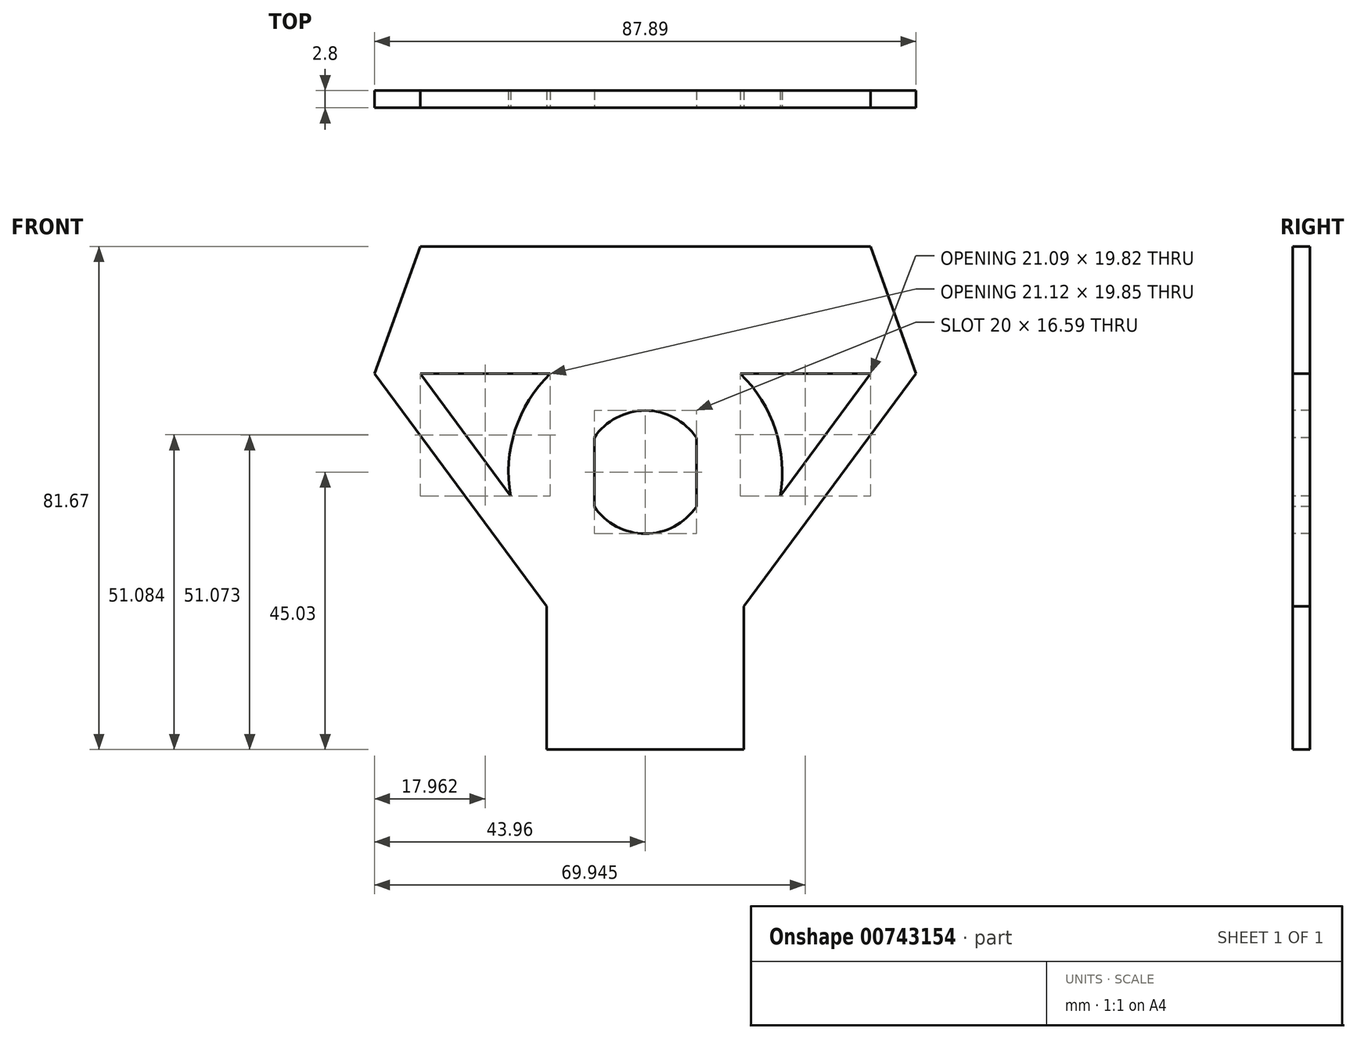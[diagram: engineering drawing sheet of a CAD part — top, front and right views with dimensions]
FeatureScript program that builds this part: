
annotation { "Feature Type Name" : "Feature", "Feature Type Description" : "" }
export const myFeature = defineFeature(function(context is Context, id is Id, definition is map)
    precondition{}
    {
        {
            var Q0;
            Q0=qCreatedBy(makeId("Front.planeOp"),FACE);
            var sketch = newSketch(context, id + "F0", { "sketchPlane" : qUnion([Q0])});
            skCircle(sketch, "E0", {"center": v(0, -32.04) * mm, "radius": 10 * mm});
            skCircle(sketch, "E1", {"center": v(0, 0) * mm, "radius": 22.21 * mm});
            skCircle(sketch, "E2", {"center": v(0, 0) * mm, "radius": 10 * mm});
            skLineSegment(sketch, "E3", {"start": v(0, -45.03) * mm, "end": v(16, -45.03) * mm});
            skLineSegment(sketch, "E4", {"start": v(0, -45.03) * mm, "end": v(-16, -45.03) * mm});
            skLineSegment(sketch, "E5", {"start": v(-16, -45.03) * mm, "end": v(-16, -21.8) * mm});
            skLineSegment(sketch, "E6", {"start": v(16, -45.03) * mm, "end": v(16, -21.8) * mm});
            skLineSegment(sketch, "E7", {"start": v(16, -21.8) * mm, "end": v(43.93, 15.97) * mm});
            skLineSegment(sketch, "E8", {"start": v(36.53, 15.97) * mm, "end": v(14.2, -14.23) * mm});
            skLineSegment(sketch, "E9", {"start": v(14.2, -14.23) * mm, "end": v(8.3, -5.59) * mm});
            skLineSegment(sketch, "E10", {"start": v(8.3, -5.59) * mm, "end": v(8.3, 15.97) * mm});
            skLineSegment(sketch, "E11", {"start": v(8.3, 15.97) * mm, "end": v(36.53, 15.97) * mm});
            skLineSegment(sketch, "E12", {"start": v(43.93, 15.97) * mm, "end": v(36.53, 36.64) * mm});
            skLineSegment(sketch, "E13", {"start": v(-16, -21.8) * mm, "end": v(-43.96, 15.97) * mm});
            skLineSegment(sketch, "E14", {"start": v(-36.56, 15.97) * mm, "end": v(-14.2, -14.23) * mm});
            skLineSegment(sketch, "E15", {"start": v(-14.2, -14.23) * mm, "end": v(-8.3, -5.59) * mm});
            skLineSegment(sketch, "E16", {"start": v(-8.3, -5.59) * mm, "end": v(-8.3, 15.97) * mm});
            skLineSegment(sketch, "E17", {"start": v(-8.3, 15.97) * mm, "end": v(-36.56, 15.97) * mm});
            skLineSegment(sketch, "E18", {"start": v(-43.96, 15.97) * mm, "end": v(-36.56, 36.64) * mm});
            skLineSegment(sketch, "E19", {"start": v(-36.56, 36.64) * mm, "end": v(36.53, 36.64) * mm});
            skSolve(sketch);
        }
        {
            var Q0;
            {var subQ0=sQuery(id+"F0.wireOp",EDGE,"E18");Q0=makeQuery(id+"F0.imprint","IMPRINT",FACE,{"disambiguationData":[TD([[makeQuery(id+"F0.imprint","IMPRINT",EDGE,{"derivedFrom":subQ0}),-1.0]])]});}
            extrude(context, id + "F1", {"entities" : qUnion([Q0]), "oppositeDirection" : true, "depth" : 2.8 * mm, "offsetDistance" : 25 * mm});
        }
        {
            var Q0;
            {var subQ0=sQuery(id+"F0.wireOp",EDGE,"E12");Q0=makeQuery(id+"F0.imprint","IMPRINT",FACE,{"disambiguationData":[TD([[makeQuery(id+"F0.imprint","IMPRINT",EDGE,{"derivedFrom":subQ0}),1.0]])]});}
            var Q1;
            {var subQ0=sQuery(id+"F0.wireOp",EDGE,"5sK9wntb-EpGf-xt0I-Ifqt-AHv8B5OIWTuE");var subQ1=sQuery(id+"F0.wireOp",EDGE,"E1");var subQ2=makeQuery(id+"F0.imprint","INTERSECT",VERTEX,{"disambiguationData":[OD(1.0)],"derivedFrom":[subQ1,subQ0]});Q1=makeQuery(id+"F0.imprint","IMPRINT",FACE,{"disambiguationData":[TD([[makeQuery(id+"F0.imprint","IMPRINT",EDGE,{"disambiguationData":[TD([[subQ2,-1.0]])],"derivedFrom":subQ1}),-1.0]])]});}
            extrude(context, id + "F2", {"entities" : qUnion([Q0, Q1]), "operationType" : NewBodyOperationType.ADD, "oppositeDirection" : true, "depth" : 2.8 * mm, "offsetDistance" : 25 * mm});
        }
        {
            var Q0;
            {var subQ0=sQuery(id+"F0.wireOp",EDGE,"E9");Q0=makeQuery(id+"F0.imprint","IMPRINT",FACE,{"disambiguationData":[TD([[makeQuery(id+"F0.imprint","IMPRINT",EDGE,{"derivedFrom":subQ0}),1.0]])]});}
            var Q1;
            Q1=makeQuery(id+"F0.imprint","IMPRINT",FACE,{"disambiguationData":[TD([[makeQuery(id+"F0.imprint","IMPRINT",EDGE,{"derivedFrom":sQuery(id+"F0.wireOp",EDGE,"E3")}),1.0]])]});
            var Q2;
            {var subQ0=sQuery(id+"F0.wireOp",EDGE,"E1");var subQ1=sQuery(id+"F0.wireOp",EDGE,"E0");var subQ2=makeQuery(id+"F0.imprint","INTERSECT",VERTEX,{"disambiguationData":[OD(0.0)],"derivedFrom":[subQ1,subQ0]});Q2=makeQuery(id+"F0.imprint","IMPRINT",FACE,{"disambiguationData":[TD([[makeQuery(id+"F0.imprint","IMPRINT",EDGE,{"disambiguationData":[TD([[subQ2,-1.0]])],"derivedFrom":subQ1}),1.0]])]});}
            extrude(context, id + "F3", {"entities" : qUnion([Q0, Q1, Q2]), "operationType" : NewBodyOperationType.ADD, "oppositeDirection" : true, "depth" : 2.8 * mm, "offsetDistance" : 25 * mm});
        }
        {
            var Q0;
            {var subQ0=sQuery(id+"F0.wireOp",EDGE,"5sK9wntb-EpGf-xt0I-Ifqt-AHv8B5OIWTuE");var subQ1=sQuery(id+"F0.wireOp",EDGE,"E1");var subQ2=makeQuery(id+"F0.imprint","INTERSECT",VERTEX,{"disambiguationData":[OD(1.0)],"derivedFrom":[subQ1,subQ0]});Q0=makeQuery(id+"F0.imprint","IMPRINT",FACE,{"disambiguationData":[TD([[makeQuery(id+"F0.imprint","IMPRINT",EDGE,{"disambiguationData":[TD([[subQ2,-1.0]])],"derivedFrom":subQ1}),1.0]])]});}
            var Q1;
            {var subQ0=sQuery(id+"F0.wireOp",EDGE,"E2");var subQ4=sQuery(id+"F0.wireOp",EDGE,"5sK9wntb-EpGf-xt0I-Ifqt-AHv8B5OIWTuE");var subQ9=makeQuery(id+"F0.imprint","INTERSECT",VERTEX,{"disambiguationData":[OD(0.0)],"derivedFrom":[subQ0,subQ4]});Q1=makeQuery(id+"F0.imprint","IMPRINT",FACE,{"disambiguationData":[TD([[makeQuery(id+"F0.imprint","IMPRINT",EDGE,{"disambiguationData":[TD([[subQ9,1.0]])],"derivedFrom":subQ0}),1.0]])]});}
            extrude(context, id + "F4", {"entities" : qUnion([Q0, Q1]), "operationType" : NewBodyOperationType.ADD, "oppositeDirection" : true, "depth" : 2.8 * mm, "offsetDistance" : 25 * mm});
        }
        {
            var Q0;
            {var subQ0=sQuery(id+"F0.wireOp",EDGE,"5sK9wntb-EpGf-xt0I-Ifqt-AHv8B5OIWTuE");var subQ1=sQuery(id+"F0.wireOp",EDGE,"E2");var subQ2=makeQuery(id+"F0.imprint","INTERSECT",VERTEX,{"disambiguationData":[OD(0.0)],"derivedFrom":[subQ1,subQ0]});Q0=makeQuery(id+"F0.imprint","IMPRINT",FACE,{"disambiguationData":[TD([[makeQuery(id+"F0.imprint","IMPRINT",EDGE,{"disambiguationData":[TD([[subQ2,1.0]])],"derivedFrom":subQ1}),-1.0]])]});}
            var Q1;
            {var subQ5=sQuery(id+"F0.wireOp",EDGE,"E1");var subQ8=sQuery(id+"F0.wireOp",EDGE,"E11");var subQ9=makeQuery(id+"F0.imprint","INTERSECT",VERTEX,{"derivedFrom":[subQ5,subQ8]});Q1=makeQuery(id+"F0.imprint","IMPRINT",FACE,{"disambiguationData":[TD([[makeQuery(id+"F0.imprint","IMPRINT",EDGE,{"disambiguationData":[TD([[subQ9,-1.0]])],"derivedFrom":subQ5}),1.0]])]});}
            var Q2;
            {var subQ0=sQuery(id+"F0.wireOp",EDGE,"mikma1tP-L6bX-YgQz-vDAg-WGWVEiNV3o0V");var subQ1=sQuery(id+"F0.wireOp",EDGE,"E1");var subQ2=makeQuery(id+"F0.imprint","INTERSECT",VERTEX,{"disambiguationData":[OD(0.0)],"derivedFrom":[subQ1,subQ0]});Q2=makeQuery(id+"F0.imprint","IMPRINT",FACE,{"disambiguationData":[TD([[makeQuery(id+"F0.imprint","IMPRINT",EDGE,{"disambiguationData":[TD([[subQ2,-1.0]])],"derivedFrom":subQ1}),1.0]])]});}
            var Q3;
            {var subQ0=sQuery(id+"F0.wireOp",EDGE,"mikma1tP-L6bX-YgQz-vDAg-WGWVEiNV3o0V");var subQ1=sQuery(id+"F0.wireOp",EDGE,"E2");var subQ2=makeQuery(id+"F0.imprint","INTERSECT",VERTEX,{"derivedFrom":[subQ1,subQ0]});Q3=makeQuery(id+"F0.imprint","IMPRINT",FACE,{"disambiguationData":[TD([[makeQuery(id+"F0.imprint","IMPRINT",EDGE,{"disambiguationData":[TD([[subQ2,-1.0]])],"derivedFrom":subQ1}),-1.0]])]});}
            extrude(context, id + "F5", {"entities" : qUnion([Q0, Q1, Q2, Q3]), "operationType" : NewBodyOperationType.ADD, "oppositeDirection" : true, "depth" : 2.8 * mm, "offsetDistance" : 25 * mm});
        }
        {
            var Q0;
            {var subQ0=sQuery(id+"F0.wireOp",EDGE,"5sK9wntb-EpGf-xt0I-Ifqt-AHv8B5OIWTuE");var subQ1=sQuery(id+"F0.wireOp",EDGE,"E2");var subQ2=makeQuery(id+"F0.imprint","INTERSECT",VERTEX,{"disambiguationData":[OD(0.0)],"derivedFrom":[subQ1,subQ0]});Q0=makeQuery(id+"F0.imprint","IMPRINT",FACE,{"disambiguationData":[TD([[makeQuery(id+"F0.imprint","IMPRINT",EDGE,{"disambiguationData":[TD([[subQ2,-1.0]])],"derivedFrom":subQ1}),1.0]])]});}
            var Q1;
            {var subQ0=sQuery(id+"F0.wireOp",EDGE,"E1");var subQ1=sQuery(id+"F0.wireOp",EDGE,"E0");var subQ2=makeQuery(id+"F0.imprint","INTERSECT",VERTEX,{"disambiguationData":[OD(0.0)],"derivedFrom":[subQ1,subQ0]});Q1=makeQuery(id+"F0.imprint","IMPRINT",FACE,{"disambiguationData":[TD([[makeQuery(id+"F0.imprint","IMPRINT",EDGE,{"disambiguationData":[TD([[subQ2,1.0]])],"derivedFrom":subQ1}),1.0]])]});}
            extrude(context, id + "F6", {"entities" : qUnion([Q0, Q1]), "operationType" : NewBodyOperationType.ADD, "oppositeDirection" : true, "depth" : 2.8 * mm, "offsetDistance" : 25 * mm});
        }
    });
